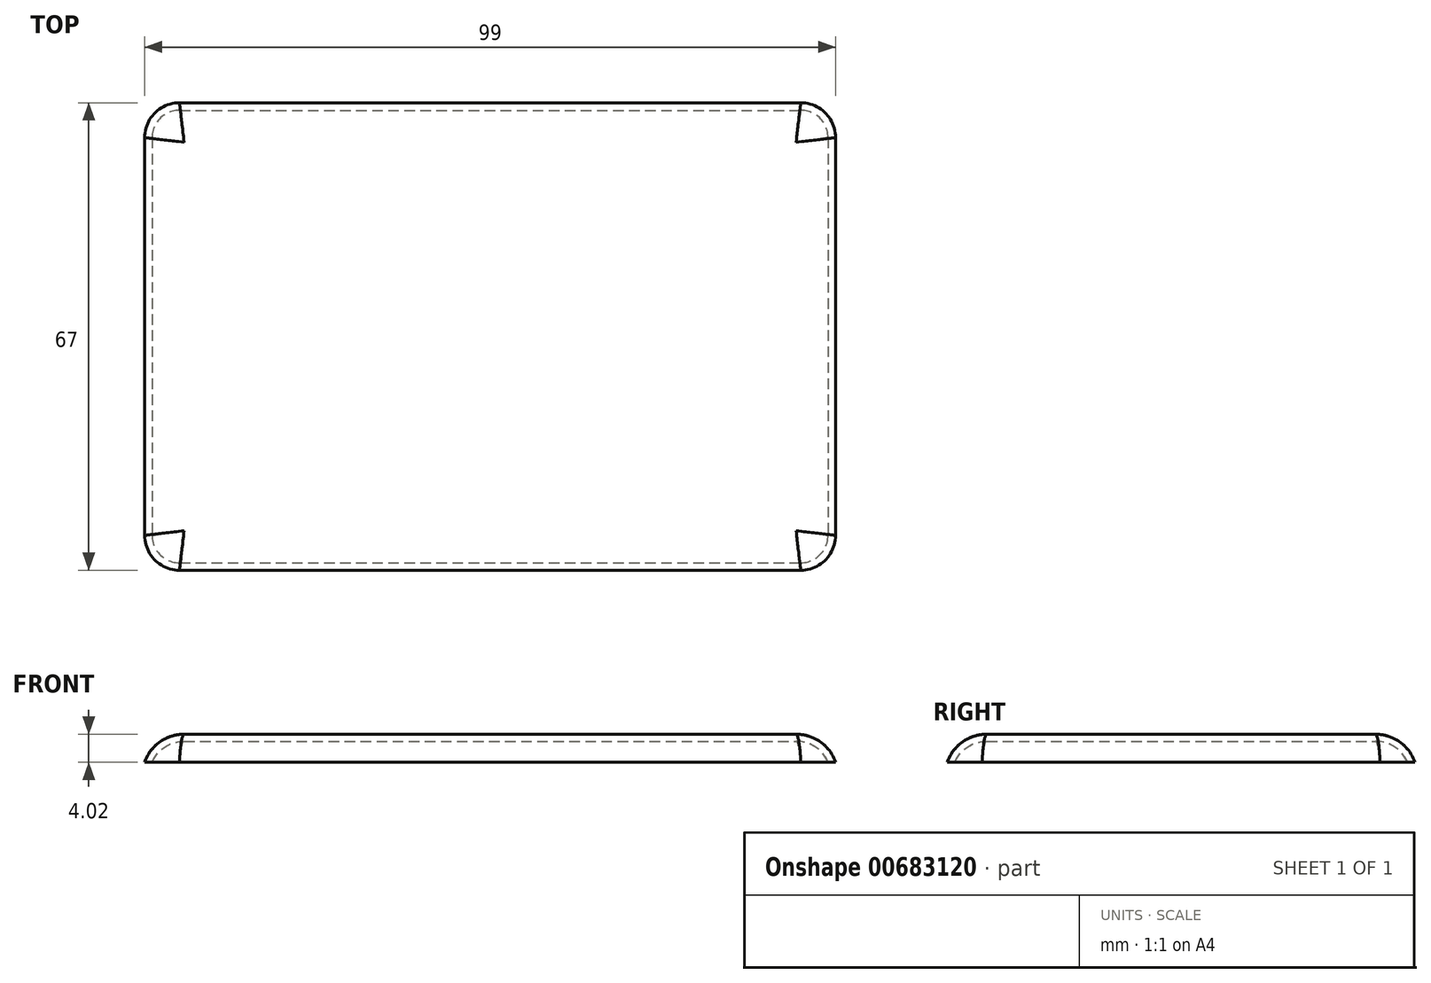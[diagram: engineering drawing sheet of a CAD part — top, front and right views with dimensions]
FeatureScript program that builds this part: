
annotation { "Feature Type Name" : "Feature", "Feature Type Description" : "" }
export const myFeature = defineFeature(function(context is Context, id is Id, definition is map)
    precondition{}
    {
        {
            var Q0;
            Q0=qCreatedBy(makeId("Top.planeOp"),FACE);
            var sketch = newSketch(context, id + "F0", { "sketchPlane" : qUnion([Q0])});
            skLineSegment(sketch, "E0.bottom", {"start": v(-44.5, 33.5) * mm, "end": v(44.5, 33.5) * mm});
            skLineSegment(sketch, "E0.top", {"start": v(-44.5, -33.5) * mm, "end": v(44.5, -33.5) * mm});
            skLineSegment(sketch, "E0.left", {"start": v(-49.5, 28.5) * mm, "end": v(-49.5, -28.5) * mm});
            skLineSegment(sketch, "E0.right", {"start": v(49.5, 28.5) * mm, "end": v(49.5, -28.5) * mm});
            skPoint(sketch, "E1", {"position": v(0, 33.5) * mm});
            skPoint(sketch, "E2", {"position": v(49.5, 0) * mm});
            skPoint(sketch, "E3", {"position": v(0, -33.5) * mm});
            skPoint(sketch, "E4", {"position": v(-49.5, 0) * mm});
            skPoint(sketch, "E5.visualSharp", {"position": v(-49.5, 33.5) * mm});
            skArc(sketch, "E5.filletArc", {"start": v(-44.5, 33.5) * mm, "mid": v(-48.04, 32.04) * mm, "end": v(-49.5, 28.5) * mm});
            skPoint(sketch, "E6.visualSharp", {"position": v(49.5, 33.5) * mm});
            skArc(sketch, "E6.filletArc", {"start": v(49.5, 28.5) * mm, "mid": v(48.04, 32.04) * mm, "end": v(44.5, 33.5) * mm});
            skPoint(sketch, "E7.visualSharp", {"position": v(49.5, -33.5) * mm});
            skArc(sketch, "E7.filletArc", {"start": v(44.5, -33.5) * mm, "mid": v(48.04, -32.04) * mm, "end": v(49.5, -28.5) * mm});
            skPoint(sketch, "E8.visualSharp", {"position": v(-49.5, -33.5) * mm});
            skArc(sketch, "E8.filletArc", {"start": v(-49.5, -28.5) * mm, "mid": v(-48.04, -32.04) * mm, "end": v(-44.5, -33.5) * mm});
            skSolve(sketch);
        }
        {
            var Q0;
            Q0=qSketchRegion(id+"F0",true);
            extrude(context, id + "F1", {"entities" : qUnion([Q0]), "depth" : 4 * mm, "offsetDistance" : 25.4 * mm});
        }
        {
            var Q0;
            Q0=makeQuery(id+"F1.opExtrude","CAP_FACE",FACE,{"disambiguationData":[OSD([sQuery(id+"F0.wireOp",EDGE,"E0.bottom"),sQuery(id+"F0.wireOp",EDGE,"E0.top"),sQuery(id+"F0.wireOp",EDGE,"E0.left"),sQuery(id+"F0.wireOp",EDGE,"E0.right"),sQuery(id+"F0.wireOp",EDGE,"E5.filletArc"),sQuery(id+"F0.wireOp",EDGE,"E6.filletArc"),sQuery(id+"F0.wireOp",EDGE,"E7.filletArc"),sQuery(id+"F0.wireOp",EDGE,"E8.filletArc")])],"isStart":false});
            fillet(context, id + "F2", {"entities" : qUnion([Q0]), "radius" : 6 * mm, "tangentPropagation" : true, "allowEdgeOverflow" : false});
        }
        {
            var Q0;
            Q0=makeQuery(id+"F1.opExtrude","CAP_FACE",FACE,{"disambiguationData":[OSD([sQuery(id+"F0.wireOp",EDGE,"E0.bottom"),sQuery(id+"F0.wireOp",EDGE,"E0.top"),sQuery(id+"F0.wireOp",EDGE,"E0.left"),sQuery(id+"F0.wireOp",EDGE,"E0.right"),sQuery(id+"F0.wireOp",EDGE,"E5.filletArc"),sQuery(id+"F0.wireOp",EDGE,"E6.filletArc"),sQuery(id+"F0.wireOp",EDGE,"E7.filletArc"),sQuery(id+"F0.wireOp",EDGE,"E8.filletArc")])],"isStart":true});
            shell(context, id + "F3", {"entities" : qUnion([Q0]), "thickness" : 1 * mm});
        }
    });
